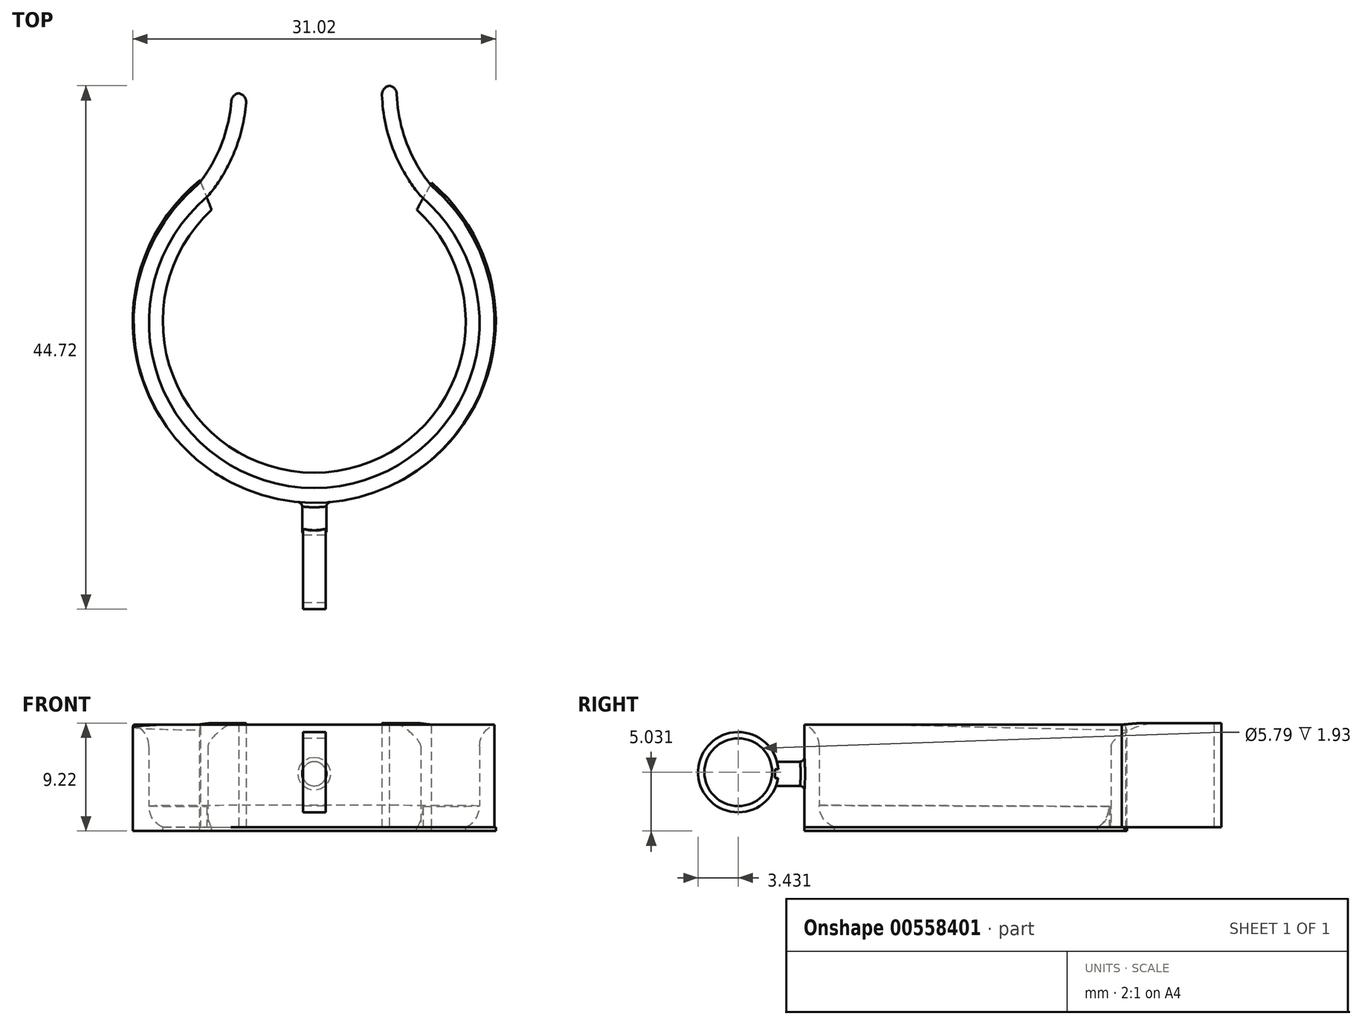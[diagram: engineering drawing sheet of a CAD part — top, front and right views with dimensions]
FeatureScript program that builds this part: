
annotation { "Feature Type Name" : "Feature", "Feature Type Description" : "" }
export const myFeature = defineFeature(function(context is Context, id is Id, definition is map)
    precondition{}
    {
        {
            var Q0;
            Q0=qCreatedBy(makeId("Top.planeOp"),FACE);
            var sketch = newSketch(context, id + "F0", { "sketchPlane" : qUnion([Q0])});
            skLineSegment(sketch, "E0", {"start": v(-9, -32.66) * mm, "end": v(9, -32.66) * mm, "construction": true});
            skLineSegment(sketch, "E1", {"start": v(-9, 27.34) * mm, "end": v(9, 27.34) * mm, "construction": true});
            skPoint(sketch, "E2.visualSharp", {"position": v(-9.44, 10.99) * mm});
            skPoint(sketch, "E3.visualSharp", {"position": v(9.44, 10.99) * mm});
            skArc(sketch, "E4.0", {"start": v(-9.09, -7.85) * mm, "mid": v(0, -32.8) * mm, "end": v(9.09, -7.85) * mm});
            skArc(sketch, "E5.0", {"start": v(-10, -6.95) * mm, "mid": v(0, -34.06) * mm, "end": v(10, -6.95) * mm});
            skArc(sketch, "E6.0", {"start": v(-9.09, -7.85) * mm, "mid": v(-6.84, -4.11) * mm, "end": v(-5.82, 0.13) * mm});
            skArc(sketch, "E7.0", {"start": v(-10, -6.95) * mm, "mid": v(-7.99, -3.57) * mm, "end": v(-7.09, 0.25) * mm});
            skArc(sketch, "E8.0", {"start": v(5.79, 0.8) * mm, "mid": v(6.71, -3.8) * mm, "end": v(9.09, -7.85) * mm});
            skArc(sketch, "E9.0", {"start": v(7.06, 0.85) * mm, "mid": v(7.88, -3.3) * mm, "end": v(10, -6.95) * mm});
            skPoint(sketch, "E10.visualSharp", {"position": v(-7.05, 0.95) * mm});
            skArc(sketch, "E10.filletArc", {"start": v(-6.46, 0.94) * mm, "mid": v(-6.9, 0.7) * mm, "end": v(-7.09, 0.25) * mm});
            skPoint(sketch, "E11.visualSharp", {"position": v(-5.78, 0.95) * mm});
            skArc(sketch, "E11.filletArc", {"start": v(-5.82, 0.13) * mm, "mid": v(-5.98, 0.66) * mm, "end": v(-6.46, 0.94) * mm});
            skPoint(sketch, "E12.visualSharp", {"position": v(5.78, 1.6) * mm});
            skArc(sketch, "E12.filletArc", {"start": v(6.42, 1.58) * mm, "mid": v(5.96, 1.31) * mm, "end": v(5.79, 0.8) * mm});
            skPoint(sketch, "E13.visualSharp", {"position": v(7.05, 1.6) * mm});
            skArc(sketch, "E13.filletArc", {"start": v(7.06, 0.85) * mm, "mid": v(6.87, 1.33) * mm, "end": v(6.42, 1.58) * mm});
            skSolve(sketch);
        }
        {
            var Q0;
            Q0 = qSketchRegion(id + "F0", true);
            extrude(context, id + "F1", {"entities" : qUnion([Q0]), "depth" : 8.9 * mm, "offsetDistance" : 25.4 * mm});
        }
        {
            var Q0;
            Q0=qCreatedBy(makeId("Top.planeOp"),FACE);
            var sketch = newSketch(context, id + "F2", { "sketchPlane" : qUnion([Q0])});
            skArc(sketch, "E14", {"start": v(-9.77, -6.5) * mm, "mid": v(-0.16, -34.05) * mm, "end": v(10.02, -6.7) * mm});
            skArc(sketch, "E15", {"start": v(-8.76, -9.02) * mm, "mid": v(0, -31.48) * mm, "end": v(8.76, -9.02) * mm});
            skLineSegment(sketch, "E16", {"start": v(-9.77, -6.5) * mm, "end": v(-8.76, -9.02) * mm});
            skLineSegment(sketch, "E17", {"start": v(10.02, -6.7) * mm, "end": v(8.76, -9.02) * mm});
            skSolve(sketch);
        }
        {
            var Q0;
            Q0 = qSketchRegion(id + "F2", true);
            extrude(context, id + "F3", {"entities" : qUnion([Q0]), "operationType" : NewBodyOperationType.ADD, "oppositeDirection" : true, "depth" : 0.33 * mm, "offsetDistance" : 25.4 * mm});
        }
        {
            var Q0;
            {var subQ0=sQuery(id+"F0.wireOp",EDGE,"E7.0");var subQ1=sQuery(id+"F2.wireOp",EDGE,"E14");var subQ2=sQuery(id+"F0.wireOp",EDGE,"E5.0");var subQ3=makeQuery(id+"F1.opExtrude","SWEPT_FACE",FACE,{"disambiguationData":[OSD([subQ2])]});var subQ4=makeQuery(id+"F3.opExtrude","CAP_FACE",FACE,{"disambiguationData":[OSD([subQ1,sQuery(id+"F2.wireOp",EDGE,"E15"),sQuery(id+"F2.wireOp",EDGE,"E16"),sQuery(id+"F2.wireOp",EDGE,"E17")])],"isStart":true});Q0=makeQuery(id+"F3.boolean.opBoolean","SPLIT",EDGE,{"disambiguationData":[topologyDisambiguationEdgeConnected([subQ3,subQ4]),TD([makeQuery(id+"F1.opExtrude","SWEPT_FACE",FACE,{"disambiguationData":[OSD([subQ0])]})])],"derivedFrom":makeQuery(id+"F1.opExtrude","CAP_EDGE",EDGE,{"disambiguationData":[OSD([subQ2])],"isStart":true})});}
            fillet(context, id + "F4", {"entities" : qUnion([Q0]), "radius" : 12.7 * mm, "tangentPropagation" : true, "allowEdgeOverflow" : false});
        }
        {
            var Q0;
            Q0=qCreatedBy(makeId("Front.planeOp"),FACE);
            cPlane(context, id + "F5", {"entities" : qUnion([Q0]), "cplaneType" : CPlaneType.OFFSET, "offset" : 33.53 * mm, "width" : 152.4 * mm, "height" : 152.4 * mm});
        }
        {
            var Q0;
            Q0=qCreatedBy(id+"F5.planeOp",FACE);
            var sketch = newSketch(context, id + "F6", { "sketchPlane" : qUnion([Q0])});
            skCircle(sketch, "E18", {"center": v(0, 4.57) * mm, "radius": 1.04 * mm});
            skSolve(sketch);
        }
        {
            var Q0;
            Q0 = qSketchRegion(id + "F6", true);
            extrude(context, id + "F7", {"entities" : qUnion([Q0]), "operationType" : NewBodyOperationType.ADD, "depth" : 3.05 * mm, "offsetDistance" : 25.4 * mm});
        }
        {
            var Q0;
            Q0=makeQuery(id+"F7.boolean.opBoolean","INTERSECT",EDGE,{"derivedFrom":[makeQuery(id+"F1.opExtrude","SWEPT_FACE",FACE,{"disambiguationData":[OSD([sQuery(id+"F0.wireOp",EDGE,"E5.0")])]}),makeQuery(id+"F7.opExtrude","SWEPT_FACE",FACE,{"disambiguationData":[OSD([sQuery(id+"F6.wireOp",EDGE,"E18")])]})]});
            fillet(context, id + "F8", {"entities" : qUnion([Q0]), "radius" : 0.38 * mm, "tangentPropagation" : true, "allowEdgeOverflow" : false});
        }
        {
            var Q0;
            Q0=makeQuery(id+"F1.opExtrude","CAP_EDGE",EDGE,{"disambiguationData":[OSD([sQuery(id+"F0.wireOp",EDGE,"E4.0")])],"isStart":false});
            fillet(context, id + "F9", {"entities" : qUnion([Q0]), "radius" : 1.98 * mm, "tangentPropagation" : true, "allowEdgeOverflow" : false});
        }
        {
            var Q0;
            {var subQ0=sQuery(id+"F0.wireOp",EDGE,"E4.0");Q0=makeQuery(id+"F3.boolean.opBoolean","SPLIT",EDGE,{"disambiguationData":[topologyDisambiguationEdgeConnected([makeQuery(id+"F1.opExtrude","SWEPT_FACE",FACE,{"disambiguationData":[OSD([subQ0])]}),makeQuery(id+"F3.opExtrude","CAP_FACE",FACE,{"disambiguationData":[OSD([sQuery(id+"F2.wireOp",EDGE,"E14"),sQuery(id+"F2.wireOp",EDGE,"E15"),sQuery(id+"F2.wireOp",EDGE,"E16"),sQuery(id+"F2.wireOp",EDGE,"E17")])],"isStart":true})])],"derivedFrom":makeQuery(id+"F1.opExtrude","CAP_EDGE",EDGE,{"disambiguationData":[OSD([subQ0])],"isStart":true})});}
            fillet(context, id + "F10", {"entities" : qUnion([Q0]), "radius" : 1.98 * mm, "tangentPropagation" : true, "allowEdgeOverflow" : false});
        }
        {
            var Q0;
            Q0=qCreatedBy(makeId("Right.planeOp"),FACE);
            var sketch = newSketch(context, id + "F11", { "sketchPlane" : qUnion([Q0])});
            skCircle(sketch, "E19", {"center": v(-39.7, 4.7) * mm, "radius": 3.43 * mm});
            skPoint(sketch, "E19.first.point", {"position": v(-36.28, 4.71) * mm});
            skPoint(sketch, "E19.second.point", {"position": v(-43.14, 4.8) * mm});
            skPoint(sketch, "E19.third.point", {"position": v(-38.23, 1.6) * mm});
            skCircle(sketch, "E20.0", {"center": v(-39.7, 4.7) * mm, "radius": 2.9 * mm});
            skSolve(sketch);
        }
        {
            var Q0;
            Q0=makeQuery(id+"F11.imprint","IMPRINT",FACE,{"disambiguationData":[TD([[makeQuery(id+"F11.imprint","IMPRINT",EDGE,{"derivedFrom":sQuery(id+"F11.wireOp",EDGE,"E19")}),1.0]])]});
            extrude(context, id + "F12", {"entities" : qUnion([Q0]), "operationType" : NewBodyOperationType.ADD, "endBound" : BoundingType.SYMMETRIC, "depth" : 1.93 * mm, "offsetDistance" : 25.4 * mm});
        }
    });
